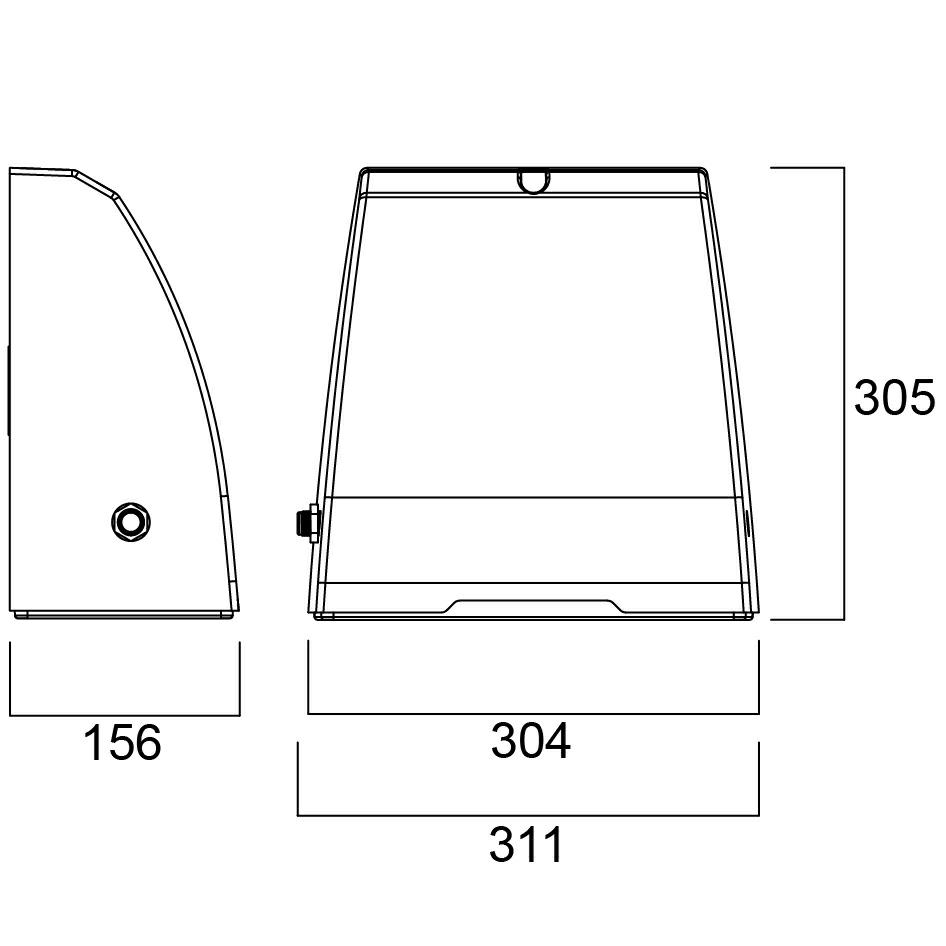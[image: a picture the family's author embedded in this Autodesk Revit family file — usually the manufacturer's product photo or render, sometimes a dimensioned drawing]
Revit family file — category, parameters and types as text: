
# Revit family: 0049945_3150lm
name_source: partatom
category: Lighting Fixtures
revit_build: Autodesk Revit 2018 (Build: 20170223_1515(x64)
units: mm (PartAtom-declared; Revit-internal decimal feet)

## family parameters
Cut with Voids When Loaded = No
Host = Face
Light Source = Yes
OmniClass Number = 23.80.70.00
OmniClass Title = Lighting
Part Type = Normal
Room Calculation Point = No
Round Connector Dimension = Use Diameter
Shared = No

## types (1)
- 0049945 MURO SURF IP65 1700-3250LM 840 PH E3 GR
    Apparent Load = 30 VA
    Assembly Code = D5020200
    AssetType = Fixed
    ClassificationName = Uniclass2015
    ClassificationValue = EF_70_80
    Color Filter = 16777215
    Cost = 0 $
    Default Elevation = 1219 mm
    Description = Muro Surface is a wall mounted fixture for exterior lighting applications with 3 hours combined non-maintained emergency unit. Comes with aluminium housing in RAL7016 anthracite grey colour, frosted PC diffuser, IP65, IK10, Class I, 4000K, non-dimmable multipower driver with 5 settings, 1700 / 1900 / 2750 / 3150 / 3250 lm, 16 / 18 / 26 / 29 / 30 W, up to 109 lm/W total system efficacy, switchable built in Mini photocell, CRI80, Asymmetrical beam, 119.000 hrs L70B50 lifespan, 304 x 305 x 155 mm (L x W x D) dimensions, 4.32 kg weight.
    Dimming Lamp Color Temperature Shift = <None>
    DocumentationLiterature = http://www.sylvania-lighting.com
    ElectricShockClassification = 108
    Emit Shape Visible in Rendering = No
    Emit from Circle Diameter = 610 mm
    IfcExportAs = Class I
    IfcExportType = IfcLightFixtureType
    ImpactProtectionIndex = IfcLightFixtureType
    IngressProtection = IfcLightFixtureType
    InputNominalFrequency = 4000
    InputVoltage = 0
    LampColourRenderingIndex = 16500
    LampColourTemperature = LED
    LampMacAdamStep = 80
    LampNominalLuminous = 4000 K
    LightOutputRatio = LED
    LuminaireType = 0
    ManufacturerName = 108 lm/W
    Material = Feilo Sylvania
    Material_1_SYL = <By Category>
    Material_2_SYL = <By Category>
    Material_3_SYL = <By Category>
    Material_4_SYL = <By Category>
    Model = Muro Surface IP65 1700-3250lm 840 PH E3 Grey
    ModelNumber = 0049945
    ModelReference = Muro Surface IP65 1700-3250lm 840 PH E3 Grey
    Name = Muro Surface IP65 1700-3250lm 840 PH E3 Grey
    NominalDepth = 155 mm  [stored 0.50853 ft]
    NominalHeight = 305 mm  [stored 1.00066 ft]
    NominalLength = 155 mm  [stored 0.50853 ft]
    Photometric Web File = 0049945_3150lm.IES
    PowerConsumption = Lighting
    PowerFactor = 0.95
    Tilt Angle = -90.00°
    Type Image = <None>
    TypeName = Muro Surface IP65 1700-3250lm 840 PH E3 Grey
    URL = 0.9
    Voltage = 0 V
    WarrantyDescription = http://www.sylvania-lighting.com

note: [stored X ft] marks values corroborated as IEEE doubles in the binary element streams (Revit-internal decimal feet)

## geometry (parser evidence)
native form markers: Sweep x1
no freeform markers — native parametric forms only
